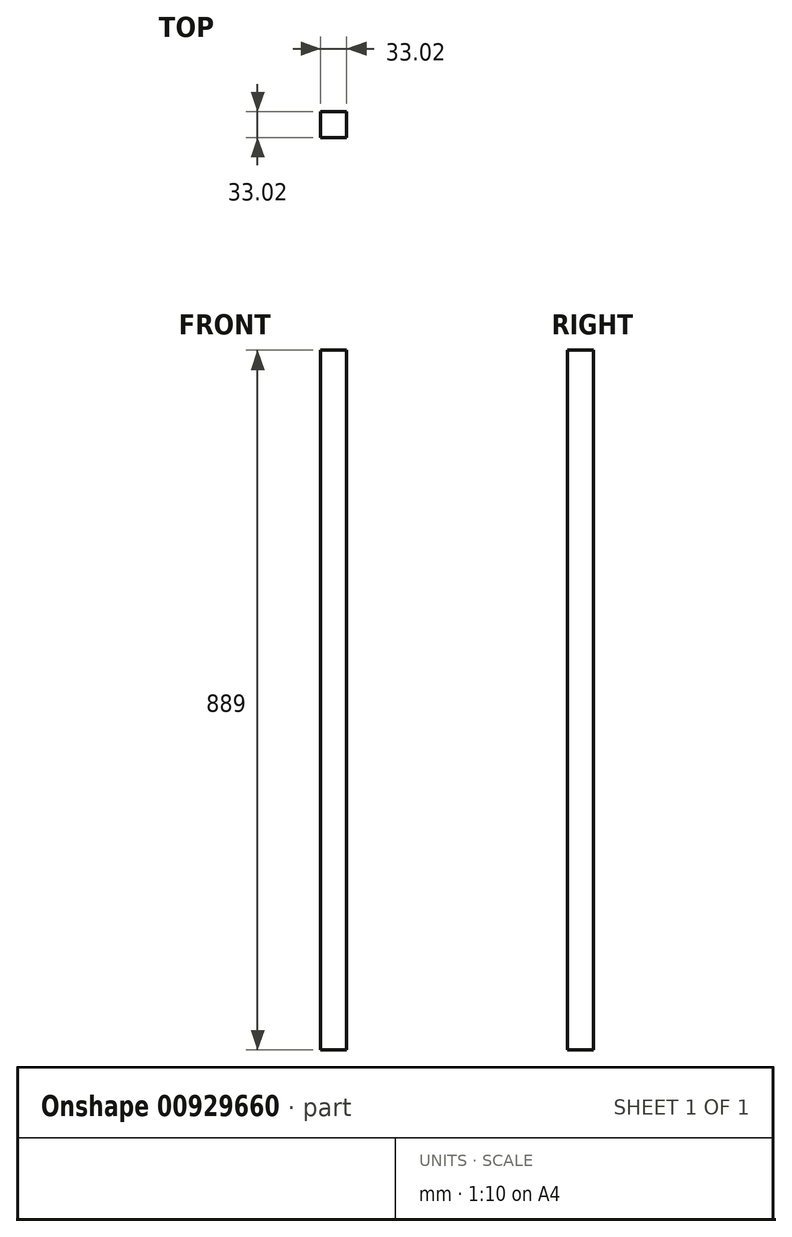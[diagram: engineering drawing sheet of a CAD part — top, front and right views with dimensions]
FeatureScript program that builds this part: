
annotation { "Feature Type Name" : "Feature", "Feature Type Description" : "" }
export const myFeature = defineFeature(function(context is Context, id is Id, definition is map)
    precondition{}
    {
        {
            var Q0;
            Q0=qCreatedBy(makeId("Front.planeOp"),FACE);
            var sketch = newSketch(context, id + "F0", { "sketchPlane" : qUnion([Q0])});
            skLineSegment(sketch, "E0.bottom", {"start": v(-65.43, 416.4) * mm, "end": v(-32.4, 416.4) * mm});
            skLineSegment(sketch, "E0.top", {"start": v(-65.43, -472.6) * mm, "end": v(-32.4, -472.6) * mm});
            skLineSegment(sketch, "E0.left", {"start": v(-65.43, 416.4) * mm, "end": v(-65.43, -472.6) * mm});
            skLineSegment(sketch, "E0.right", {"start": v(-32.4, 416.4) * mm, "end": v(-32.4, -472.6) * mm});
            skSolve(sketch);
        }
        {
            var Q0;
            Q0=makeQuery(id+"F0.imprint","IMPRINT",FACE,{"disambiguationData":[TD([[makeQuery(id+"F0.imprint","IMPRINT",EDGE,{"derivedFrom":sQuery(id+"F0.wireOp",EDGE,"E0.bottom")}),-1.0]])]});
            extrude(context, id + "F1", {"entities" : qUnion([Q0]), "depth" : 33.02 * mm, "offsetDistance" : 25.4 * mm});
        }
    });
